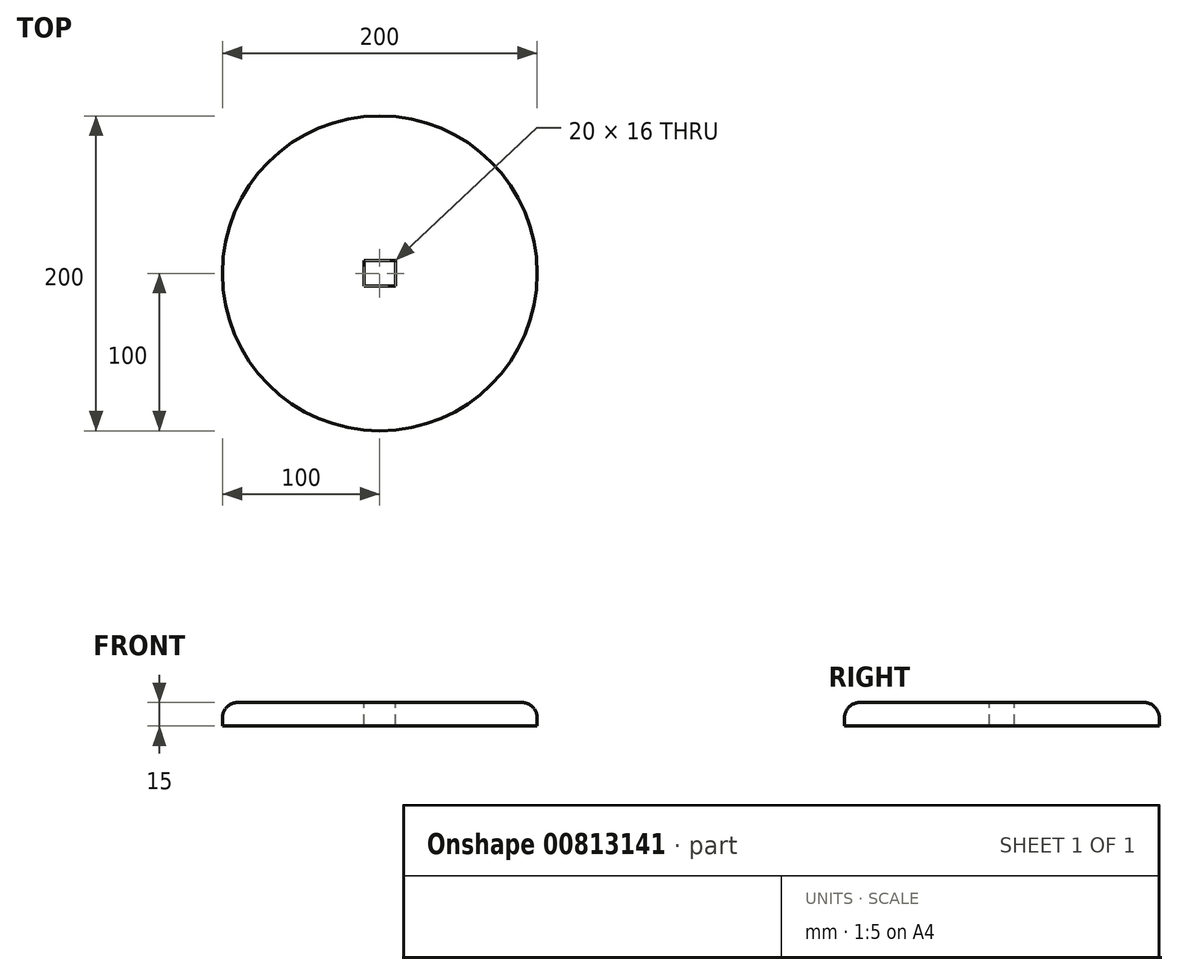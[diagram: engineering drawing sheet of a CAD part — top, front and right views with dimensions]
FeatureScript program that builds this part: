
annotation { "Feature Type Name" : "Feature", "Feature Type Description" : "" }
export const myFeature = defineFeature(function(context is Context, id is Id, definition is map)
    precondition{}
    {
        {
            var Q0;
            Q0=qCreatedBy(makeId("Top.planeOp"),FACE);
            var sketch = newSketch(context, id + "F0", { "sketchPlane" : qUnion([Q0])});
            skCircle(sketch, "E0", {"center": v(0, 0) * mm, "radius": 100 * mm});
            skSolve(sketch);
        }
        {
            var Q0;
            Q0=makeQuery(id+"F0.imprint","IMPRINT",FACE,{"disambiguationData":[TD([[makeQuery(id+"F0.imprint","IMPRINT",EDGE,{"derivedFrom":sQuery(id+"F0.wireOp",EDGE,"E0")}),1.0]])]});
            extrude(context, id + "F1", {"entities" : qUnion([Q0]), "depth" : 15 * mm, "offsetDistance" : 25 * mm});
        }
        {
            var Q0;
            Q0=makeQuery(id+"F1.opExtrude","CAP_EDGE",EDGE,{"disambiguationData":[OSD([sQuery(id+"F0.wireOp",EDGE,"E0")])],"isStart":false});
            fillet(context, id + "F2", {"entities" : qUnion([Q0]), "radius" : 10 * mm, "tangentPropagation" : true, "allowEdgeOverflow" : false});
        }
        {
            var Q0;
            Q0=makeQuery(id+"F1.opExtrude","CAP_FACE",FACE,{"disambiguationData":[OSD([sQuery(id+"F0.wireOp",EDGE,"E0")])],"isStart":false});
            var sketch = newSketch(context, id + "F3", { "sketchPlane" : qUnion([Q0])});
            skLineSegment(sketch, "E1.bottom", {"start": v(-10, -8) * mm, "end": v(10, -8) * mm});
            skLineSegment(sketch, "E1.top", {"start": v(-10, 8) * mm, "end": v(10, 8) * mm});
            skLineSegment(sketch, "E1.left", {"start": v(-10, -8) * mm, "end": v(-10, 8) * mm});
            skLineSegment(sketch, "E1.right", {"start": v(10, -8) * mm, "end": v(10, 8) * mm});
            skSolve(sketch);
        }
        {
            var Q0;
            Q0 = qSketchRegion(id + "F3", true);
            extrude(context, id + "F4", {"entities" : qUnion([Q0]), "operationType" : NewBodyOperationType.REMOVE, "oppositeDirection" : true, "depth" : 50 * mm, "offsetDistance" : 25 * mm});
        }
    });
